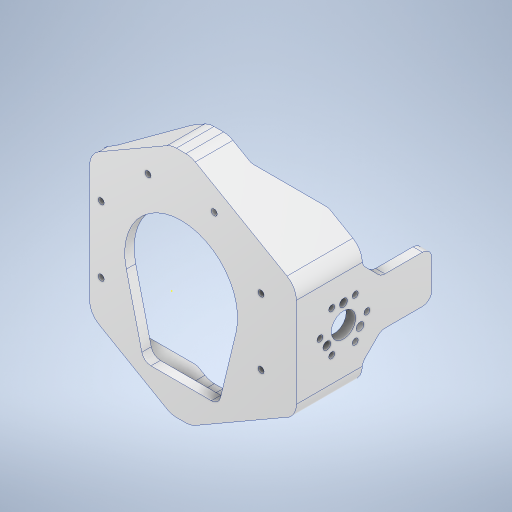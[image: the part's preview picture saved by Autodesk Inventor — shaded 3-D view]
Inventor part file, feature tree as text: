
AUTODESK INVENTOR PART (.ipt)
format: ipt  version: 2024.3 (Build 283343000, 343)  size: 827,392 bytes
history: native  units: mm
features: sketch x19, extrude x15, fillet x4, hole x3, projected_geometry x3, other x1, mirror x1
ambient origin geometry x8: Origin, YZ Plane, XZ Plane, XY Plane, X Axis, Y Axis, Z Axis, Center Point
bodies: Body1 (feature_tree)
feature tree (46):
  other  "ソリッド1"
  extrude  "押し出し1"  Depth=5.0mm TaperAngle=0.0deg
  hole  "穴1"  [1 undecoded]
  extrude  "押し出し2"  TaperAngle=22.5deg  [1 undecoded]
  extrude  "押し出し13"  Depth=80.0mm TaperAngle=360.0deg
  hole  "穴5"  [1 undecoded]
  hole  "穴6"  [1 undecoded]
  extrude  "押し出し14"  Depth=50.0mm
  extrude  "押し出し21"  Depth=65.0mm
  sketch  "スケッチ35"
  extrude  "押し出し28"  Depth=60.0mm TaperAngle=360.0deg
  extrude  "押し出し31"  Depth=65.0mm
  extrude  "押し出し32"  Depth=50.0mm
  extrude  "押し出し33"  Depth=65.0mm
  extrude  "押し出し34"  Depth=5.0mm TaperAngle=0.0deg
  extrude  "押し出し35"  Depth=60.0mm TaperAngle=360.0deg
  fillet  "フィレット28"  Radius=25.0mm
  fillet  "フィレット29"  [1 undecoded]
  extrude  "押し出し36"  Depth=30.0mm TaperAngle=360.0deg
  extrude  "押し出し37"  Depth=25.0mm
  extrude  "押し出し38"  TaperAngle=0.0deg  [1 undecoded]
  fillet  "フィレット32"  Radius=13.0mm
  fillet  "フィレット33"  Radius=32.5mm
  mirror  "ミラー1"
  extrude  "押し出し39"  Depth=25.0mm
  sketch  "スケッチ1"
  sketch  "スケッチ2"
  sketch  "スケッチ3"
  sketch  "スケッチ17"
  sketch  "スケッチ18"
  sketch  "スケッチ19"
  sketch  "スケッチ20"
  sketch  "スケッチ28"
  sketch  "スケッチ36"
  projected_geometry  "投影ループ1"
  sketch  "スケッチ39"
  sketch  "スケッチ40"
  sketch  "スケッチ42"
  sketch  "スケッチ43"
  sketch  "スケッチ45"
  projected_geometry  "投影ループ2"
  sketch  "スケッチ46"
  projected_geometry  "投影ループ3"
  sketch  "スケッチ47"
  sketch  "スケッチ48"
  sketch  "スケッチ49"
note: 6 required parameter values undecoded (feature->parameter linkage not recoverable at this tier; creation-order binding heuristic only, values carry confidence <= 0.55)
